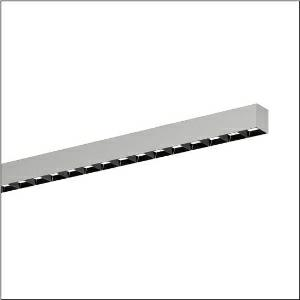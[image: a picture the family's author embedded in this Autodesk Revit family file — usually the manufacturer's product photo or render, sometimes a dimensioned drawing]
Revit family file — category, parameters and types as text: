
# Revit family: silica_r__21_51mx21tat4s_03ed
name_source: partatom
category: Lighting Fixtures
units: mm (PartAtom-declared; Revit-internal decimal feet)

## family parameters
Cut with Voids When Loaded = No
Host = Face
Light Source = No
Part Type = Normal
Room Calculation Point = No
Round Connector Dimension = Use Diameter
Shared = No

## types (1)
- --- (1 x LED, 3720 lm, 32.2 W, 6500K)
    Apparent Load = 32 VA
    CIE Flux Codes = 85 99 100 100 100
    Color Rendering = 80
    Color Temperature = 6500K
    Default Elevation = 1800 mm
    Description = Silica® 21, office luminaire, primary light control with darklight reflector, of PMMA, black, CAT 2 (L<= 3000cd/m²), light emission: direct distribution, primary light characteristic: symmetric, installation type: surface-mounted, LED, rated luminous flux: 3.720lm, luminous efficacy: 110lm/W, light colour: 8tw, colour temperature: 2700..6500K, control gear: DALI DT8, with terminal, 3+2-pole, max. 2.5mm², mains connection: 220..240V, AC, 50/60Hz, rated input power: 33.8W, luminaire housing, of aluminium, metallic grey (RAL 9006), length: 1.204mm, width: 53mm, height: 53mm, protection rating (complete): IP20, insulation class (complete): insulation class I (protective earthing), certification: CE, permissible operating ambient temperature: 0..+35°C, standard: EN 50419, packaging unit: 1 piece
    Height = 53 mm
    Lamp = 1 x LED
    Lamp Light Flux = 3720 lm
    Lamp Power = 32.2 W
    Lamp count = 1
    Length = 1204 mm
    Luminous efficacy = 116 lm/W
    Manufacturer = Siteco
    ModVariant = No
    Model = 51MX21TAT4S
    Mounting Place = Ceiling
    Mounting Type = Surface mounted
    Number of Poles = 1
    OnlyDefault = Yes
    Power Factor = 1
    Product Name = Silica® 21
    Product group = office luminaire | ceiling mounted
    ProductGroupID = 303
    Protection Class = Protection class I
    Protection Degree = IP 20
    RLX_Detail_Level = 1
    RLX_Emergency_Light_Flux = 0 lm
    RLX_Emergency_Type = 0
    RLX_Emergency_Type_DB = No
    RlxData = <blob elided: 39213 chars, md5=d8601750>
    Socket = socket
    Standby Power = 0 W
    System Light Flux = 3720 lm
    System Power = 32 W
    Type Comments = individual setting
    Type Image = l_1335929.jpg
    URL = http://relux.com
    VarID = @adj_161531
    Voltage = 0 V
    Weight = 0.00 kg
    Width = 53 mm

## geometry (parser evidence)
native form markers: Blend x4, Sweep x10
no freeform markers — native parametric forms only
